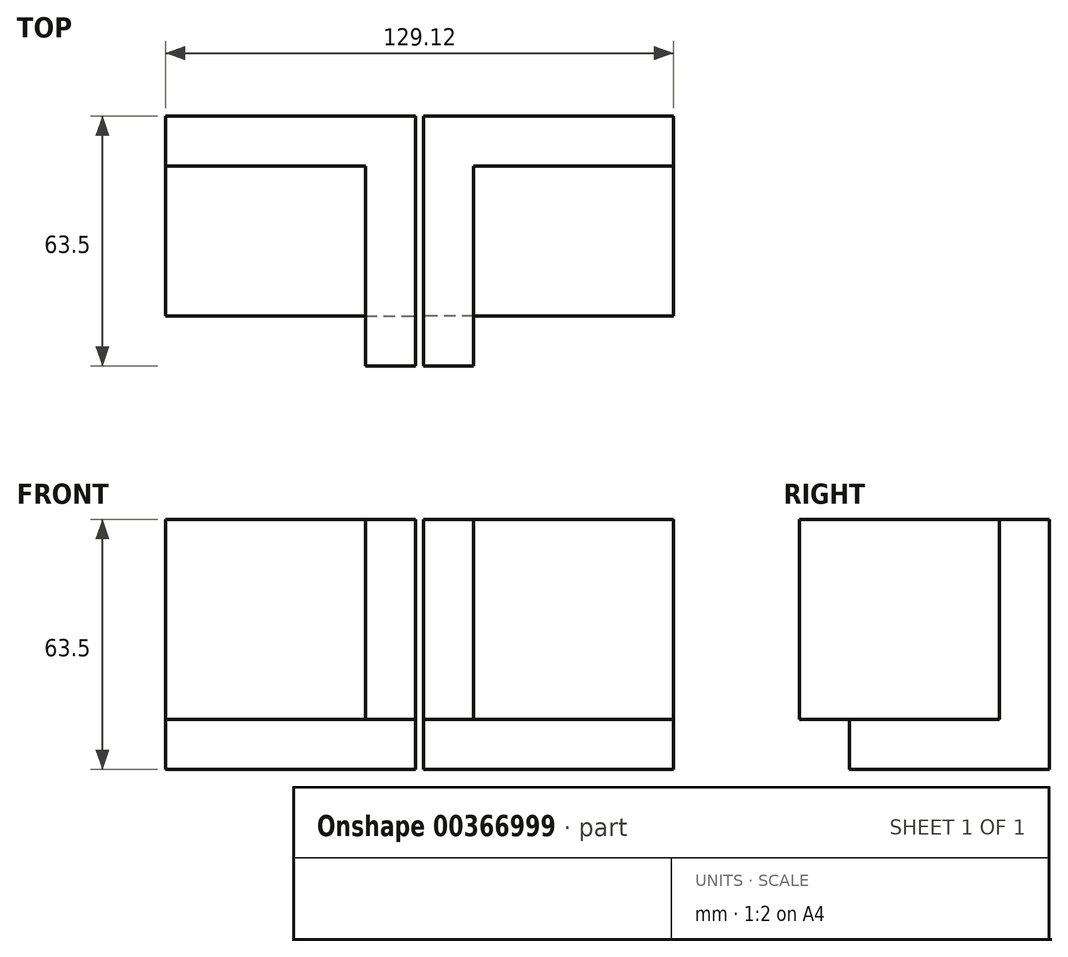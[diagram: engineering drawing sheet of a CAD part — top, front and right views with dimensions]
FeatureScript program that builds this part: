
annotation { "Feature Type Name" : "Feature", "Feature Type Description" : "" }
export const myFeature = defineFeature(function(context is Context, id is Id, definition is map)
    precondition{}
    {
        {
            var Q0;
            Q0=qCreatedBy(makeId("Top.planeOp"),FACE);
            var sketch = newSketch(context, id + "F0", { "sketchPlane" : qUnion([Q0])});
            skLineSegment(sketch, "E0.bottom", {"start": v(-64.56, -64.4) * mm, "end": v(-1.06, -64.4) * mm});
            skLineSegment(sketch, "E0.top", {"start": v(-64.56, -13.6) * mm, "end": v(-1.06, -13.6) * mm});
            skLineSegment(sketch, "E0.left", {"start": v(-64.56, -64.4) * mm, "end": v(-64.56, -13.6) * mm});
            skLineSegment(sketch, "E0.right", {"start": v(-1.06, -64.4) * mm, "end": v(-1.06, -13.6) * mm});
            skLineSegment(sketch, "E1.bottom", {"start": v(-51.86, -64.4) * mm, "end": v(-1.06, -64.4) * mm});
            skLineSegment(sketch, "E1.top", {"start": v(-51.86, -77.1) * mm, "end": v(-1.06, -77.1) * mm});
            skLineSegment(sketch, "E1.left", {"start": v(-51.86, -64.4) * mm, "end": v(-51.86, -77.1) * mm});
            skLineSegment(sketch, "E1.right", {"start": v(-1.06, -64.4) * mm, "end": v(-1.06, -77.1) * mm});
            skSolve(sketch);
        }
        {
            var Q0;
            Q0=makeQuery(id+"F0.imprint","IMPRINT",FACE,{"disambiguationData":[TD([[makeQuery(id+"F0.imprint","IMPRINT",EDGE,{"derivedFrom":sQuery(id+"F0.wireOp",EDGE,"E1.bottom")}),-1.0]])]});
            var Q1;
            Q1=makeQuery(id+"F0.imprint","IMPRINT",FACE,{"disambiguationData":[TD([[makeQuery(id+"F0.imprint","IMPRINT",EDGE,{"derivedFrom":sQuery(id+"F0.wireOp",EDGE,"E0.bottom")}),1.0]])]});
            extrude(context, id + "F1", {"entities" : qUnion([Q0, Q1]), "depth" : 12.7 * mm});
        }
        {
            var Q0;
            Q0=makeQuery(id+"F1.opExtrude","CAP_FACE",FACE,{"disambiguationData":[OSD([sQuery(id+"F0.wireOp",EDGE,"E0.bottom"),sQuery(id+"F0.wireOp",EDGE,"E0.top"),sQuery(id+"F0.wireOp",EDGE,"E0.left"),sQuery(id+"F0.wireOp",EDGE,"E0.right"),sQuery(id+"F0.wireOp",EDGE,"E1.top"),sQuery(id+"F0.wireOp",EDGE,"E1.left"),sQuery(id+"F0.wireOp",EDGE,"E1.right")])],"isStart":false});
            var sketch = newSketch(context, id + "F2", { "sketchPlane" : qUnion([Q0])});
            skLineSegment(sketch, "E2.bottom", {"start": v(-64.56, -13.6) * mm, "end": v(-1.06, -13.6) * mm});
            skLineSegment(sketch, "E2.top", {"start": v(-64.56, -26.3) * mm, "end": v(-1.06, -26.3) * mm});
            skLineSegment(sketch, "E2.left", {"start": v(-64.56, -13.6) * mm, "end": v(-64.56, -26.3) * mm});
            skLineSegment(sketch, "E2.right", {"start": v(-1.06, -13.6) * mm, "end": v(-1.06, -26.3) * mm});
            skSolve(sketch);
        }
        {
            var Q0;
            Q0=qSketchRegion(id+"F2",true);
            extrude(context, id + "F3", {"entities" : qUnion([Q0]), "operationType" : NewBodyOperationType.ADD, "depth" : 50.8 * mm});
        }
        {
            var Q0;
            Q0=makeQuery(id+"F3.opExtrude","SWEPT_FACE",FACE,{"disambiguationData":[OSD([sQuery(id+"F2.wireOp",EDGE,"E2.top")])]});
            var sketch = newSketch(context, id + "F4", { "sketchPlane" : qUnion([Q0])});
            skLineSegment(sketch, "E3.bottom", {"start": v(-1.06, 12.7) * mm, "end": v(-13.76, 12.7) * mm});
            skLineSegment(sketch, "E3.top", {"start": v(-1.06, 63.5) * mm, "end": v(-13.76, 63.5) * mm});
            skLineSegment(sketch, "E3.left", {"start": v(-1.06, 12.7) * mm, "end": v(-1.06, 63.5) * mm});
            skLineSegment(sketch, "E3.right", {"start": v(-13.76, 12.7) * mm, "end": v(-13.76, 63.5) * mm});
            skSolve(sketch);
        }
        {
            var Q0;
            Q0=qSketchRegion(id+"F4",true);
            extrude(context, id + "F5", {"entities" : qUnion([Q0]), "operationType" : NewBodyOperationType.ADD, "depth" : 50.8 * mm});
        }
        {
            var Q0;
            Q0=makeQuery(id+"F1.opExtrude","SWEPT_BODY",BODY,{"disambiguationData":[OSD([sQuery(id+"F0.wireOp",EDGE,"E0.bottom"),sQuery(id+"F0.wireOp",EDGE,"E0.top"),sQuery(id+"F0.wireOp",EDGE,"E0.left"),sQuery(id+"F0.wireOp",EDGE,"E0.right"),sQuery(id+"F0.wireOp",EDGE,"E1.top"),sQuery(id+"F0.wireOp",EDGE,"E1.left"),sQuery(id+"F0.wireOp",EDGE,"E1.right")])]});
            var Q1;
            Q1=qCreatedBy(makeId("Right.planeOp"),FACE);
            mirror(context, id + "F6", {"entities" : qUnion([Q0]), "mirrorPlane" : qUnion([Q1])});
        }
    });
